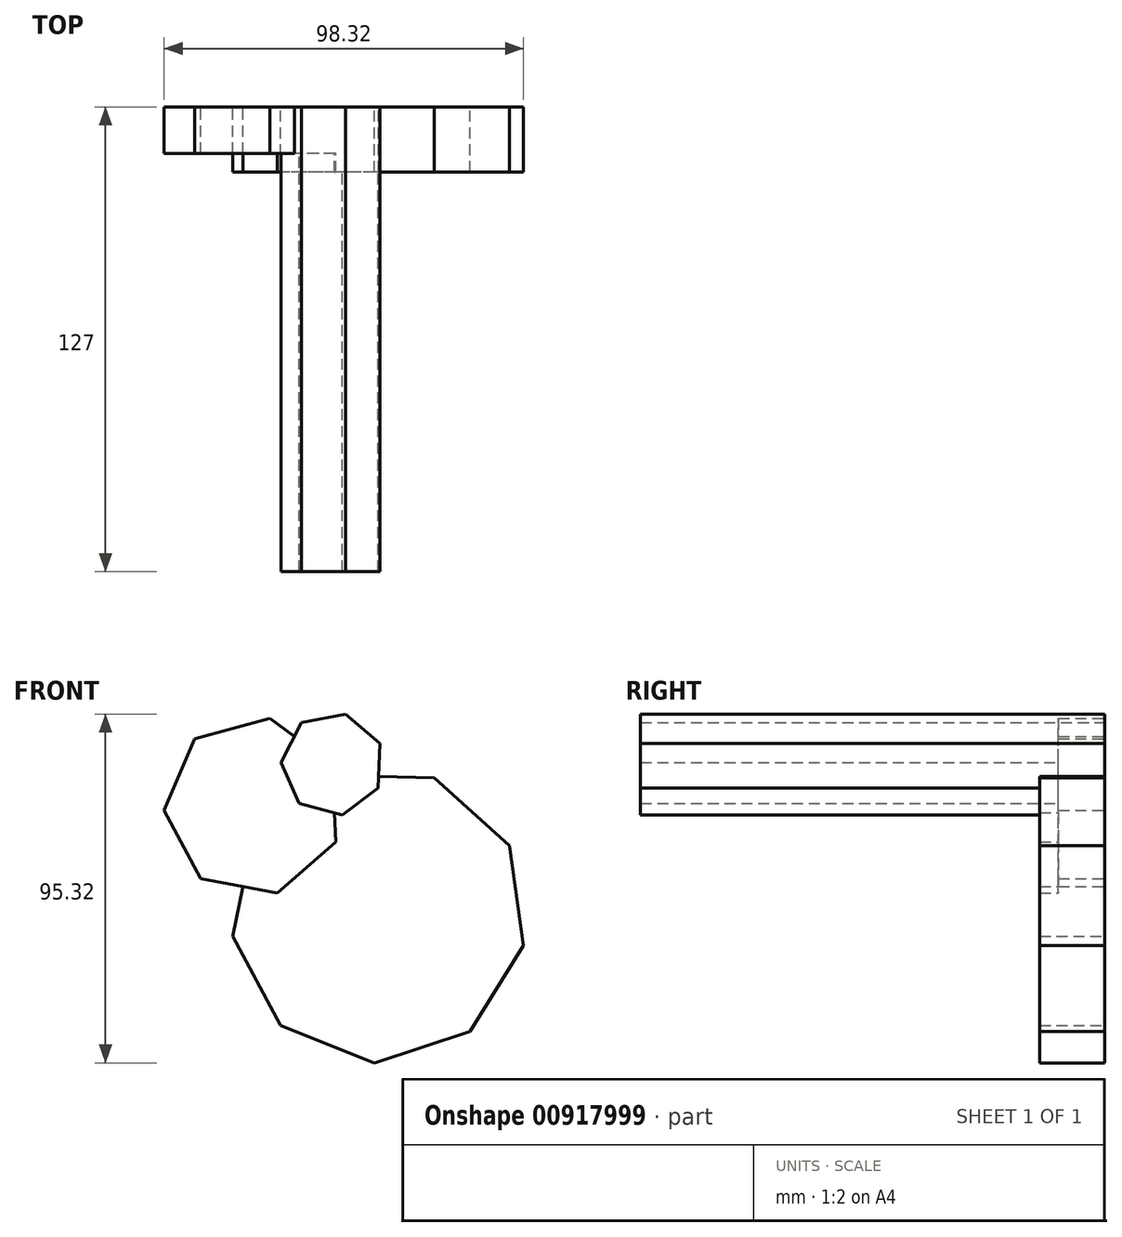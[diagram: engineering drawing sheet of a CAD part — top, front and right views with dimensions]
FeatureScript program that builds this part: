
annotation { "Feature Type Name" : "Feature", "Feature Type Description" : "" }
export const myFeature = defineFeature(function(context is Context, id is Id, definition is map)
    precondition{}
    {
        {
            var Q0;
            Q0=qCreatedBy(makeId("Front.planeOp"),FACE);
            var sketch = newSketch(context, id + "F0", { "sketchPlane" : qUnion([Q0])});
            skCircle(sketch, "E0.cCircle", {"center": v(0, 0) * mm, "radius": 37.97 * mm, "construction": true});
            skLineSegment(sketch, "E0.0", {"start": v(-1.33, -40.38) * mm, "end": v(-26.98, -30.08) * mm});
            skLineSegment(sketch, "E0.1", {"start": v(-26.98, -30.08) * mm, "end": v(-40, -5.7) * mm});
            skLineSegment(sketch, "E0.2", {"start": v(-40, -5.7) * mm, "end": v(-34.3, 21.35) * mm});
            skLineSegment(sketch, "E0.3", {"start": v(-34.3, 21.35) * mm, "end": v(-12.56, 38.4) * mm});
            skLineSegment(sketch, "E0.4", {"start": v(-12.56, 38.4) * mm, "end": v(15.07, 37.5) * mm});
            skLineSegment(sketch, "E0.5", {"start": v(15.07, 37.5) * mm, "end": v(35.64, 19.04) * mm});
            skLineSegment(sketch, "E0.6", {"start": v(35.64, 19.04) * mm, "end": v(39.54, -8.33) * mm});
            skLineSegment(sketch, "E0.7", {"start": v(39.54, -8.33) * mm, "end": v(24.94, -31.8) * mm});
            skLineSegment(sketch, "E0.8", {"start": v(24.94, -31.8) * mm, "end": v(-1.33, -40.38) * mm});
            skPoint(sketch, "E0.0.midPoint", {"position": v(-14.16, -35.23) * mm});
            skCircle(sketch, "E1.cCircle", {"center": v(-34.3, 29.72) * mm, "radius": 22.07 * mm, "construction": true});
            skLineSegment(sketch, "E1.0", {"start": v(-11.8, 20.05) * mm, "end": v(-27.84, 6.1) * mm});
            skLineSegment(sketch, "E1.1", {"start": v(-27.84, 6.1) * mm, "end": v(-48.74, 9.93) * mm});
            skLineSegment(sketch, "E1.2", {"start": v(-48.74, 9.93) * mm, "end": v(-58.78, 28.67) * mm});
            skLineSegment(sketch, "E1.3", {"start": v(-58.78, 28.67) * mm, "end": v(-50.39, 48.2) * mm});
            skLineSegment(sketch, "E1.4", {"start": v(-50.39, 48.2) * mm, "end": v(-29.89, 53.8) * mm});
            skLineSegment(sketch, "E1.5", {"start": v(-29.89, 53.8) * mm, "end": v(-12.71, 41.28) * mm});
            skLineSegment(sketch, "E1.6", {"start": v(-12.71, 41.28) * mm, "end": v(-11.8, 20.05) * mm});
            skPoint(sketch, "E1.0.midPoint", {"position": v(-19.82, 13.07) * mm});
            skCircle(sketch, "E2.cCircle", {"center": v(-12.71, 41.28) * mm, "radius": 12.72 * mm, "construction": true});
            skLineSegment(sketch, "E2.0", {"start": v(0.2, 46.98) * mm, "end": v(-0.2, 34.74) * mm});
            skLineSegment(sketch, "E2.1", {"start": v(-0.2, 34.74) * mm, "end": v(-10.03, 27.42) * mm});
            skLineSegment(sketch, "E2.2", {"start": v(-10.03, 27.42) * mm, "end": v(-21.88, 30.54) * mm});
            skLineSegment(sketch, "E2.3", {"start": v(-21.88, 30.54) * mm, "end": v(-26.83, 41.75) * mm});
            skLineSegment(sketch, "E2.4", {"start": v(-26.83, 41.75) * mm, "end": v(-21.15, 52.6) * mm});
            skLineSegment(sketch, "E2.5", {"start": v(-21.15, 52.6) * mm, "end": v(-9.12, 54.94) * mm});
            skLineSegment(sketch, "E2.6", {"start": v(-9.12, 54.94) * mm, "end": v(0.2, 46.98) * mm});
            skPoint(sketch, "E2.0.midPoint", {"position": v(0, 40.86) * mm});
            skSolve(sketch);
        }
        {
            var Q0;
            Q0=makeQuery(id+"F0.imprint","IMPRINT",FACE,{"disambiguationData":[TD([[makeQuery(id+"F0.imprint","IMPRINT",EDGE,{"derivedFrom":sQuery(id+"F0.wireOp",EDGE,"E0.0")}),-1.0]])]});
            extrude(context, id + "F1", {"entities" : qUnion([Q0]), "depth" : 17.78 * mm, "offsetDistance" : 25.4 * mm});
        }
        {
            var Q0;
            {var subQ0=sQuery(id+"F0.wireOp",EDGE,"E1.2");Q0=makeQuery(id+"F0.imprint","IMPRINT",FACE,{"disambiguationData":[TD([[makeQuery(id+"F0.imprint","IMPRINT",EDGE,{"derivedFrom":subQ0}),-1.0]])]});}
            var Q1;
            {var subQ1=sQuery(id+"F0.wireOp",EDGE,"E1.0");Q1=makeQuery(id+"F0.imprint","IMPRINT",FACE,{"disambiguationData":[TD([[makeQuery(id+"F0.imprint","IMPRINT",EDGE,{"derivedFrom":subQ1}),-1.0]])]});}
            extrude(context, id + "F2", {"entities" : qUnion([Q0, Q1]), "operationType" : NewBodyOperationType.ADD, "depth" : 12.7 * mm, "offsetDistance" : 25.4 * mm});
        }
        {
            var Q0;
            {var subQ11=sQuery(id+"F0.wireOp",EDGE,"E2.5");Q0=makeQuery(id+"F0.imprint","IMPRINT",FACE,{"disambiguationData":[TD([[makeQuery(id+"F0.imprint","IMPRINT",EDGE,{"derivedFrom":subQ11}),-1.0]])]});}
            var Q1;
            {var subQ0=sQuery(id+"F0.wireOp",EDGE,"E2.1");Q1=makeQuery(id+"F0.imprint","IMPRINT",FACE,{"disambiguationData":[TD([[makeQuery(id+"F0.imprint","IMPRINT",EDGE,{"derivedFrom":subQ0}),-1.0]])]});}
            var Q2;
            {var subQ3=sQuery(id+"F0.wireOp",EDGE,"E0.3");var subQ6=sQuery(id+"F0.wireOp",EDGE,"E2.3");var subQ8=makeQuery(id+"F0.imprint","INTERSECT",VERTEX,{"derivedFrom":[subQ3,subQ6]});Q2=makeQuery(id+"F0.imprint","IMPRINT",FACE,{"disambiguationData":[TD([[makeQuery(id+"F0.imprint","IMPRINT",EDGE,{"disambiguationData":[TD([[subQ8,-1.0]])],"derivedFrom":subQ3}),1.0]])]});}
            var Q3;
            {var subQ0=sQuery(id+"F0.wireOp",EDGE,"E2.3");var subQ1=sQuery(id+"F0.wireOp",EDGE,"E0.3");var subQ2=makeQuery(id+"F0.imprint","INTERSECT",VERTEX,{"derivedFrom":[subQ1,subQ0]});Q3=makeQuery(id+"F0.imprint","IMPRINT",FACE,{"disambiguationData":[TD([[makeQuery(id+"F0.imprint","IMPRINT",EDGE,{"disambiguationData":[TD([[subQ2,-1.0]])],"derivedFrom":subQ1}),-1.0]])]});}
            extrude(context, id + "F3", {"entities" : qUnion([Q0, Q1, Q2, Q3]), "operationType" : NewBodyOperationType.ADD, "depth" : 127 * mm, "offsetDistance" : 25.4 * mm});
        }
        {
            var Q0;
            {var subQ3=sQuery(id+"F0.wireOp",EDGE,"E0.3");var subQ6=sQuery(id+"F0.wireOp",EDGE,"E2.3");var subQ8=makeQuery(id+"F0.imprint","INTERSECT",VERTEX,{"derivedFrom":[subQ3,subQ6]});Q0=makeQuery(id+"F0.imprint","IMPRINT",FACE,{"disambiguationData":[TD([[makeQuery(id+"F0.imprint","IMPRINT",EDGE,{"disambiguationData":[TD([[subQ8,-1.0]])],"derivedFrom":subQ3}),1.0]])]});}
            var Q1;
            {var subQ11=sQuery(id+"F0.wireOp",EDGE,"E2.5");Q1=makeQuery(id+"F0.imprint","IMPRINT",FACE,{"disambiguationData":[TD([[makeQuery(id+"F0.imprint","IMPRINT",EDGE,{"derivedFrom":subQ11}),-1.0]])]});}
            var Q2;
            {var subQ0=sQuery(id+"F0.wireOp",EDGE,"E2.1");Q2=makeQuery(id+"F0.imprint","IMPRINT",FACE,{"disambiguationData":[TD([[makeQuery(id+"F0.imprint","IMPRINT",EDGE,{"derivedFrom":subQ0}),-1.0]])]});}
            var Q3;
            {var subQ0=sQuery(id+"F0.wireOp",EDGE,"E2.3");var subQ1=sQuery(id+"F0.wireOp",EDGE,"E0.3");var subQ2=makeQuery(id+"F0.imprint","INTERSECT",VERTEX,{"derivedFrom":[subQ1,subQ0]});Q3=makeQuery(id+"F0.imprint","IMPRINT",FACE,{"disambiguationData":[TD([[makeQuery(id+"F0.imprint","IMPRINT",EDGE,{"disambiguationData":[TD([[subQ2,-1.0]])],"derivedFrom":subQ1}),-1.0]])]});}
            extrude(context, id + "F4", {"entities" : qUnion([Q0, Q1, Q2, Q3]), "operationType" : NewBodyOperationType.REMOVE, "oppositeDirection" : true, "depth" : 50.8 * mm, "offsetDistance" : 25.4 * mm});
        }
    });
